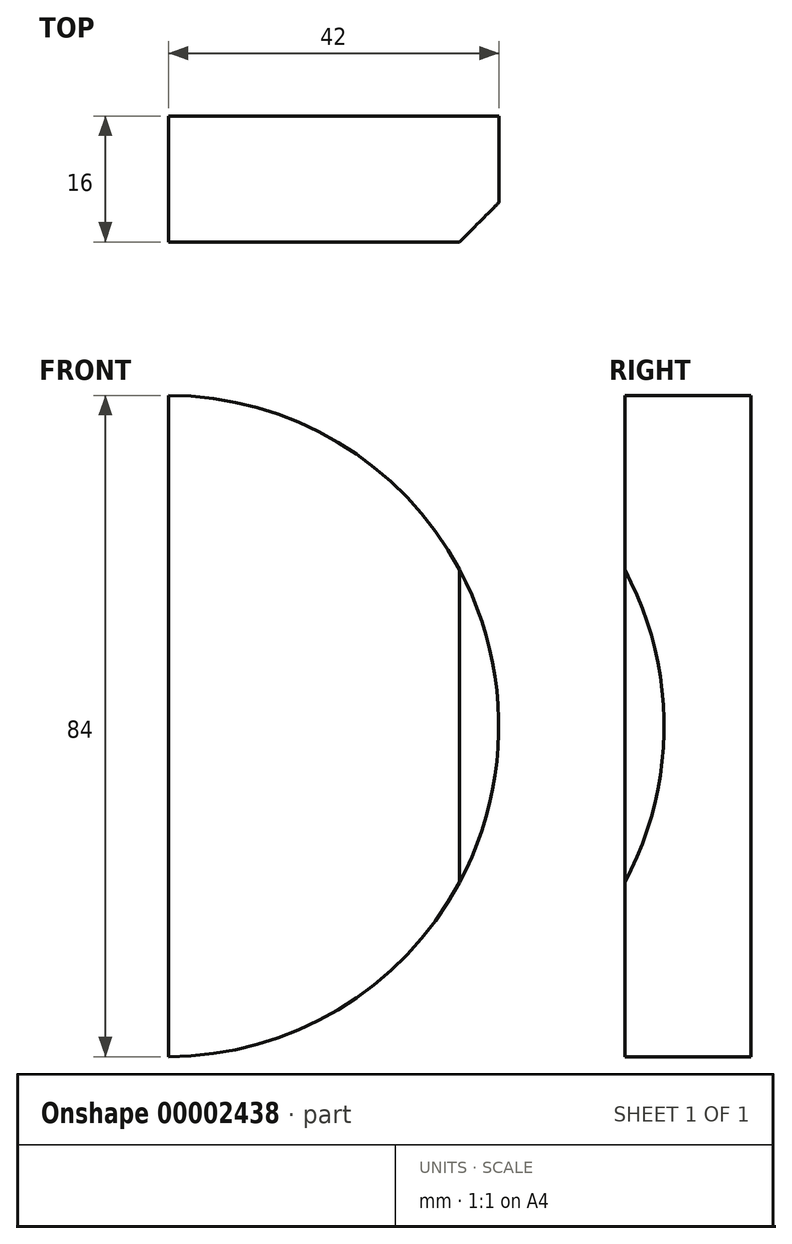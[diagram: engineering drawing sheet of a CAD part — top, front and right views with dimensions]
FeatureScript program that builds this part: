
annotation { "Feature Type Name" : "Feature", "Feature Type Description" : "" }
export const myFeature = defineFeature(function(context is Context, id is Id, definition is map)
    precondition{}
    {
        {
            var Q0;
            Q0=qCreatedBy(makeId("Top.planeOp"),FACE);
            var sketch = newSketch(context, id + "F0", { "sketchPlane" : qUnion([Q0])});
            skLineSegment(sketch, "E0.rect.bottom", {"start": v(42, 8) * mm, "end": v(-42, 8) * mm});
            skLineSegment(sketch, "E0.rect.top", {"start": v(42, -8) * mm, "end": v(-42, -8) * mm});
            skLineSegment(sketch, "E0.rect.left", {"start": v(42, 8) * mm, "end": v(42, -3) * mm});
            skLineSegment(sketch, "E0.rect.right", {"start": v(-42, 8) * mm, "end": v(-42, -8) * mm});
            skPoint(sketch, "E0.rect.middle", {"position": v(0, 0) * mm});
            skLineSegment(sketch, "E1", {"start": v(0, -36.08) * mm, "end": v(0, 34.87) * mm});
            skLineSegment(sketch, "E2", {"start": v(42, -3) * mm, "end": v(37, -8) * mm});
            skLineSegment(sketch, "E3", {"start": v(42, -3) * mm, "end": v(42, -8) * mm});
            skSolve(sketch);
        }
        {
            var Q0;
            {var subQ5=sQuery(id+"F0.wireOp",EDGE,"E0.rect.left");Q0=makeQuery(id+"F0.imprint","IMPRINT",FACE,{"disambiguationData":[TD([[makeQuery(id+"F0.imprint","IMPRINT",EDGE,{"derivedFrom":subQ5}),-1.0]])]});}
            var Q1;
            {var subQ5=sQuery(id+"F0.wireOp",EDGE,"E0.rect.left");Q1=makeQuery(id+"F0.imprint","IMPRINT",FACE,{"disambiguationData":[TD([[makeQuery(id+"F0.imprint","IMPRINT",EDGE,{"derivedFrom":subQ5}),-1.0]])]});}
            var Q2;
            {var subQ1=sQuery(id+"F0.wireOp",EDGE,"E2");Q2=makeQuery(id+"F0.imprint","IMPRINT",FACE,{"disambiguationData":[TD([[makeQuery(id+"F0.imprint","IMPRINT",EDGE,{"derivedFrom":subQ1}),1.0]])]});}
            var Q3;
            Q3=sQuery(id+"F0.wireOp",EDGE,"E1");
            revolve(context, id + "F1", {"entities" : qUnion([Q0, Q1, Q2]), "axis" : qUnion([Q3]), "revolveType" : RevolveType.SYMMETRIC, "angle" : 180 * degree});
        }
        {
            var Q0;
            Q0=sQuery(id+"F0.wireOp",EDGE,"E2");
            extrude(context, id + "F2", {"bodyType" : ToolBodyType.SURFACE, "surfaceEntities" : qUnion([Q0]), "endBound" : BoundingType.SYMMETRIC, "depth" : 50 * mm});
        }
        {
            var Q0;
            Q0=makeQuery(id+"F2.opExtrude","SWEPT_FACE",FACE,{"disambiguationData":[OSD([sQuery(id+"F0.wireOp",EDGE,"E2")])]});
            extrude(context, id + "F3", {"entities" : qUnion([Q0]), "operationType" : NewBodyOperationType.REMOVE, "oppositeDirection" : true, "depth" : 25 * mm});
        }
        {
            var Q0;
            Q0=sQuery(id+"F0.wireOp",EDGE,"E0.rect.left");
            var Q1;
            Q1=sQuery(id+"F0.wireOp",EDGE,"E3");
            var Q2;
            Q2=sQuery(id+"F0.wireOp",EDGE,"E1");
            revolve(context, id + "F4", {"bodyType" : ToolBodyType.SURFACE, "surfaceEntities" : qUnion([Q0, Q1]), "axis" : qUnion([Q2]), "revolveType" : RevolveType.FULL});
        }
    });
